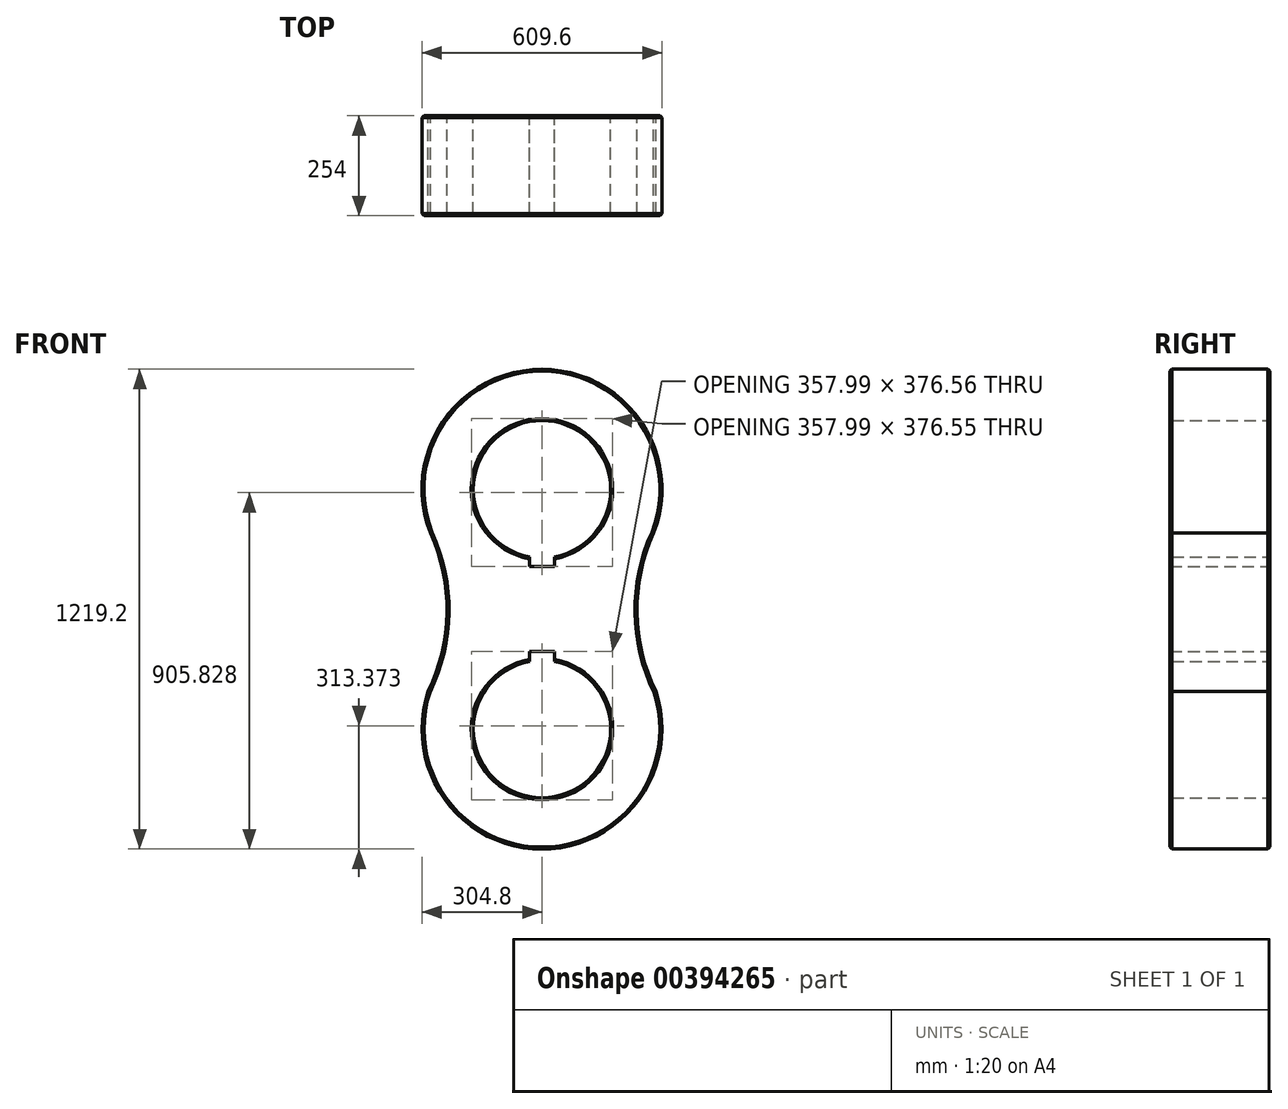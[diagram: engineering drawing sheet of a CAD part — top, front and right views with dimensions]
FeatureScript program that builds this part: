
annotation { "Feature Type Name" : "Feature", "Feature Type Description" : "" }
export const myFeature = defineFeature(function(context is Context, id is Id, definition is map)
    precondition{}
    {
        {
            var Q0;
            Q0=qCreatedBy(makeId("Front.planeOp"),FACE);
            var sketch = newSketch(context, id + "F0", { "sketchPlane" : qUnion([Q0])});
            skArc(sketch, "E0", {"start": v(-269.55, 142.3) * mm, "mid": v(0, -304.8) * mm, "end": v(269.55, 142.3) * mm});
            skLineSegment(sketch, "E1", {"start": v(-304.8, 0) * mm, "end": v(304.8, 0) * mm, "construction": true});
            skLineSegment(sketch, "E2", {"start": v(-308.27, 609.6) * mm, "end": v(363.8, 609.6) * mm, "construction": true});
            skLineSegment(sketch, "E3", {"start": v(0, 0) * mm, "end": v(0, 609.6) * mm, "construction": true});
            skArc(sketch, "E4", {"start": v(275.92, 480.1) * mm, "mid": v(0, 914.4) * mm, "end": v(-275.92, 480.1) * mm});
            skLineSegment(sketch, "E5", {"start": v(-241.3, 186.22) * mm, "end": v(-241.3, 609.6) * mm, "construction": true});
            skLineSegment(sketch, "E6", {"start": v(241.3, 0) * mm, "end": v(241.3, 609.6) * mm, "construction": true});
            skArc(sketch, "E7", {"start": v(283.66, 498.07) * mm, "mid": v(241.34, 296.15) * mm, "end": v(289.44, 95.52) * mm});
            skPoint(sketch, "E7.first.point", {"position": v(269.55, 142.3) * mm});
            skPoint(sketch, "E7.second.point", {"position": v(241.3, 304.8) * mm});
            skPoint(sketch, "E7.third.point", {"position": v(275.92, 480.1) * mm});
            skArc(sketch, "E8.MirrorC", {"start": v(-283.66, 498.07) * mm, "mid": v(-241.34, 296.15) * mm, "end": v(-289.44, 95.52) * mm});
            skPoint(sketch, "E9.orphan", {"position": v(-241.3, 0) * mm});
            skCircle(sketch, "E10", {"center": v(0, 609.6) * mm, "radius": 174.63 * mm});
            skCircle(sketch, "E11", {"center": v(0, 0) * mm, "radius": 174.63 * mm});
            skSolve(sketch);
        }
        {
            var Q0;
            Q0=makeQuery(id+"F0.imprint","IMPRINT",FACE,{"disambiguationData":[TD([[makeQuery(id+"F0.imprint","IMPRINT",EDGE,{"derivedFrom":sQuery(id+"F0.wireOp",EDGE,"E10")}),-1.0]])]});
            extrude(context, id + "F1", {"entities" : qUnion([Q0]), "depth" : 254 * mm});
        }
        {
            var Q0;
            Q0=makeQuery(id+"F1.opExtrude","CAP_EDGE",EDGE,{"disambiguationData":[OSD([sQuery(id+"F0.wireOp",EDGE,"E4")])],"isStart":false});
            var Q1;
            Q1=makeQuery(id+"F1.opExtrude","CAP_EDGE",EDGE,{"disambiguationData":[OSD([sQuery(id+"F0.wireOp",EDGE,"E8.MirrorC")])],"isStart":false});
            var Q2;
            Q2=makeQuery(id+"F1.opExtrude","CAP_EDGE",EDGE,{"disambiguationData":[OSD([sQuery(id+"F0.wireOp",EDGE,"E0")])],"isStart":false});
            var Q3;
            Q3=makeQuery(id+"F1.opExtrude","CAP_EDGE",EDGE,{"disambiguationData":[OSD([sQuery(id+"F0.wireOp",EDGE,"E7")])],"isStart":false});
            chamfer(context, id + "F2", {"entities" : qUnion([Q0, Q1, Q2, Q3]), "width" : 5.08 * mm, "tangentPropagation" : true});
        }
        {
            var Q0;
            Q0=makeQuery(id+"F1.opExtrude","CAP_EDGE",EDGE,{"disambiguationData":[OSD([sQuery(id+"F0.wireOp",EDGE,"E4")])],"isStart":true});
            var Q1;
            Q1=makeQuery(id+"F1.opExtrude","CAP_EDGE",EDGE,{"disambiguationData":[OSD([sQuery(id+"F0.wireOp",EDGE,"E8.MirrorC")])],"isStart":true});
            var Q2;
            Q2=makeQuery(id+"F1.opExtrude","CAP_EDGE",EDGE,{"disambiguationData":[OSD([sQuery(id+"F0.wireOp",EDGE,"E7")])],"isStart":true});
            var Q3;
            Q3=makeQuery(id+"F1.opExtrude","CAP_EDGE",EDGE,{"disambiguationData":[OSD([sQuery(id+"F0.wireOp",EDGE,"E0")])],"isStart":true});
            chamfer(context, id + "F3", {"entities" : qUnion([Q0, Q1, Q2, Q3]), "width" : 5.08 * mm, "tangentPropagation" : true});
        }
        {
            var Q0;
            Q0=makeQuery(id+"F1.opExtrude","CAP_EDGE",EDGE,{"disambiguationData":[OSD([sQuery(id+"F0.wireOp",EDGE,"E10")])],"isStart":true});
            chamfer(context, id + "F4", {"entities" : qUnion([Q0]), "width" : 5.08 * mm, "tangentPropagation" : true});
        }
        {
            var Q0;
            Q0=makeQuery(id+"F1.opExtrude","CAP_EDGE",EDGE,{"disambiguationData":[OSD([sQuery(id+"F0.wireOp",EDGE,"E11")])],"isStart":true});
            chamfer(context, id + "F5", {"entities" : qUnion([Q0]), "width" : 5.08 * mm, "tangentPropagation" : true});
        }
        {
            var Q0;
            Q0=makeQuery(id+"F1.opExtrude","CAP_EDGE",EDGE,{"disambiguationData":[OSD([sQuery(id+"F0.wireOp",EDGE,"E10")])],"isStart":false});
            var Q1;
            Q1=makeQuery(id+"F1.opExtrude","CAP_EDGE",EDGE,{"disambiguationData":[OSD([sQuery(id+"F0.wireOp",EDGE,"E11")])],"isStart":false});
            chamfer(context, id + "F6", {"entities" : qUnion([Q0, Q1]), "width" : 5.08 * mm, "tangentPropagation" : true});
        }
        {
            var Q0;
            Q0=makeQuery(id+"F0.imprint","IMPRINT",FACE,{"disambiguationData":[TD([[makeQuery(id+"F0.imprint","IMPRINT",EDGE,{"derivedFrom":sQuery(id+"F0.wireOp",EDGE,"E10")}),-1.0]])]});
            var sketch = newSketch(context, id + "F7", { "sketchPlane" : qUnion([Q0])});
            skCircle(sketch, "E12", {"center": v(0, 0) * mm, "radius": 174.63 * mm, "construction": true});
            skCircle(sketch, "E13", {"center": v(0, 609.6) * mm, "radius": 174.63 * mm, "construction": true});
            skLineSegment(sketch, "E14", {"start": v(31.75, 606.67) * mm, "end": v(31.75, 0) * mm, "construction": true});
            skLineSegment(sketch, "E15", {"start": v(-31.75, 610.25) * mm, "end": v(-31.75, 0) * mm, "construction": true});
            skLineSegment(sketch, "E16", {"start": v(0, 434.98) * mm, "end": v(-239.03, 434.98) * mm, "construction": true});
            skLineSegment(sketch, "E17", {"start": v(0, 434.98) * mm, "end": v(242.43, 434.98) * mm, "construction": true});
            skLineSegment(sketch, "E18", {"start": v(-239.03, 457.2) * mm, "end": v(238.11, 457.2) * mm, "construction": true});
            skLineSegment(sketch, "E19", {"start": v(-239.03, 412.75) * mm, "end": v(238.11, 412.75) * mm, "construction": true});
            skLineSegment(sketch, "E20", {"start": v(0, 174.63) * mm, "end": v(-244.84, 174.63) * mm, "construction": true});
            skLineSegment(sketch, "E21", {"start": v(0, 174.63) * mm, "end": v(242.05, 174.63) * mm, "construction": true});
            skLineSegment(sketch, "E22", {"start": v(-244.84, 196.85) * mm, "end": v(242.05, 196.85) * mm, "construction": true});
            skLineSegment(sketch, "E23", {"start": v(242.05, 152.4) * mm, "end": v(-225.62, 152.4) * mm, "construction": true});
            skLineSegment(sketch, "E24.bottom", {"start": v(-31.75, 412.75) * mm, "end": v(31.75, 412.75) * mm});
            skLineSegment(sketch, "E24.top", {"start": v(-31.75, 457.2) * mm, "end": v(31.75, 457.2) * mm});
            skLineSegment(sketch, "E24.left", {"start": v(-31.75, 412.75) * mm, "end": v(-31.75, 457.2) * mm});
            skLineSegment(sketch, "E24.right", {"start": v(31.75, 412.75) * mm, "end": v(31.75, 457.2) * mm});
            skLineSegment(sketch, "E25.bottom", {"start": v(-31.75, 152.4) * mm, "end": v(31.75, 152.4) * mm});
            skLineSegment(sketch, "E25.top", {"start": v(-31.75, 196.85) * mm, "end": v(31.75, 196.85) * mm});
            skLineSegment(sketch, "E25.left", {"start": v(-31.75, 152.4) * mm, "end": v(-31.75, 196.85) * mm});
            skLineSegment(sketch, "E25.right", {"start": v(31.75, 152.4) * mm, "end": v(31.75, 196.85) * mm});
            skSolve(sketch);
        }
        {
            var Q0;
            {var subQ0=sQuery(id+"F7.wireOp",EDGE,"E24.bottom");Q0=makeQuery(id+"F7.imprint","IMPRINT",FACE,{"disambiguationData":[TD([[makeQuery(id+"F7.imprint","IMPRINT",EDGE,{"derivedFrom":subQ0}),1.0]])]});}
            var Q1;
            {var subQ0=sQuery(id+"F7.wireOp",EDGE,"E24.top");Q1=makeQuery(id+"F7.imprint","IMPRINT",FACE,{"disambiguationData":[TD([[makeQuery(id+"F7.imprint","IMPRINT",EDGE,{"derivedFrom":subQ0}),-1.0]])]});}
            var Q2;
            {var subQ0=sQuery(id+"F7.wireOp",EDGE,"E25.top");Q2=makeQuery(id+"F7.imprint","IMPRINT",FACE,{"disambiguationData":[TD([[makeQuery(id+"F7.imprint","IMPRINT",EDGE,{"derivedFrom":subQ0}),-1.0]])]});}
            var Q3;
            {var subQ0=sQuery(id+"F7.wireOp",EDGE,"E25.bottom");Q3=makeQuery(id+"F7.imprint","IMPRINT",FACE,{"disambiguationData":[TD([[makeQuery(id+"F7.imprint","IMPRINT",EDGE,{"derivedFrom":subQ0}),1.0]])]});}
            extrude(context, id + "F8", {"entities" : qUnion([Q0, Q1, Q2, Q3]), "operationType" : NewBodyOperationType.REMOVE, "depth" : 254 * mm});
        }
    });
